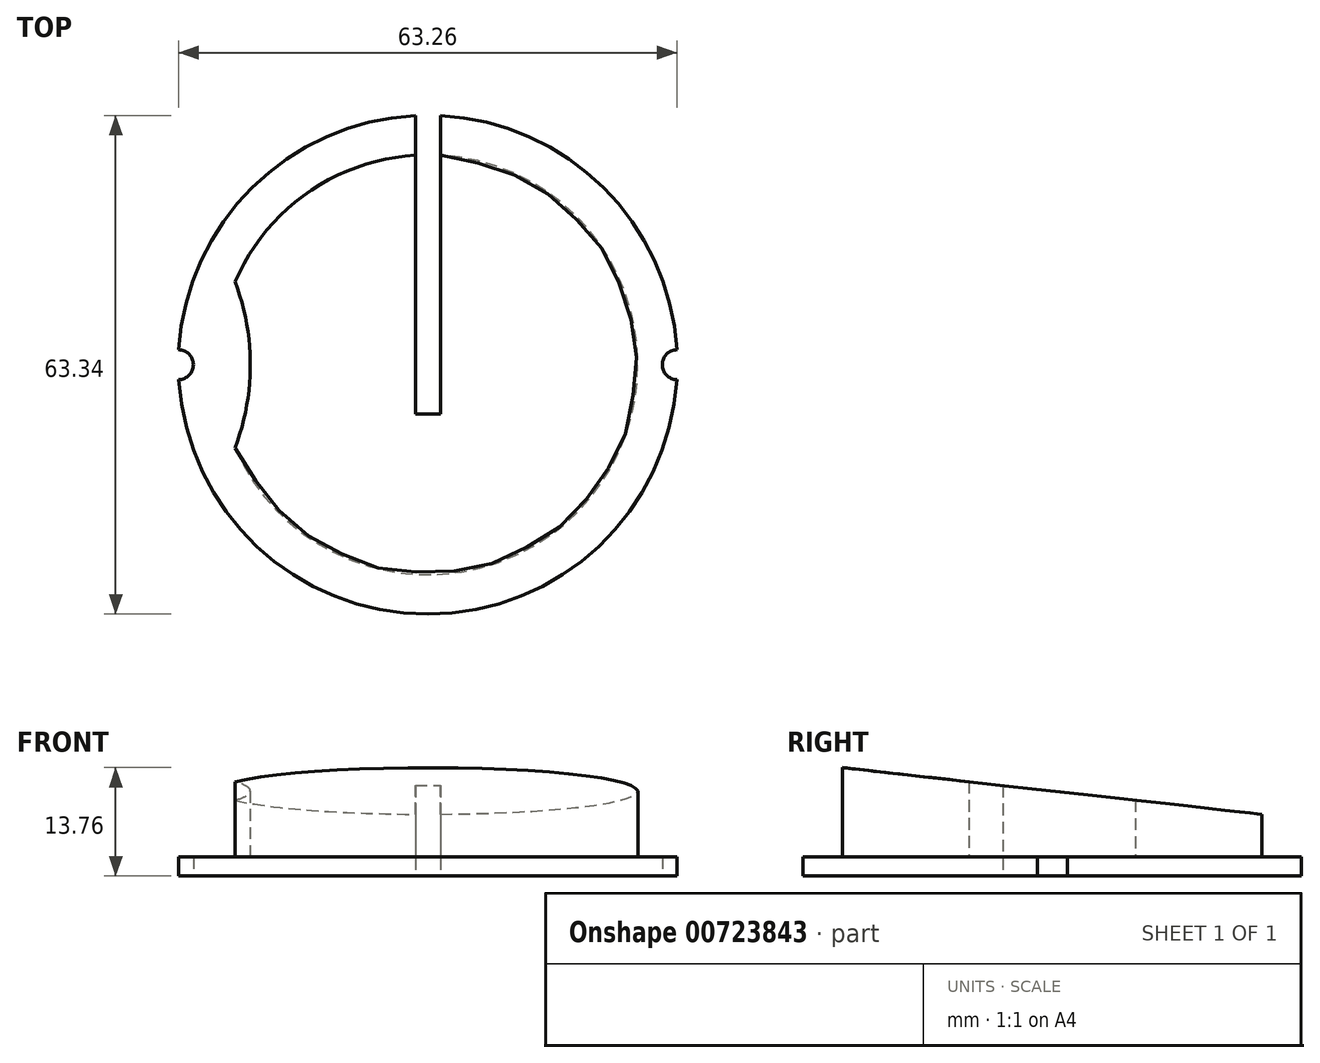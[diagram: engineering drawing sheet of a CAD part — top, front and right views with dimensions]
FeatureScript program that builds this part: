
annotation { "Feature Type Name" : "Feature", "Feature Type Description" : "" }
export const myFeature = defineFeature(function(context is Context, id is Id, definition is map)
    precondition{}
    {
        {
            var Q0;
            Q0=qCreatedBy(makeId("Top.planeOp"),FACE);
            var sketch = newSketch(context, id + "F0", { "sketchPlane" : qUnion([Q0])});
            skArc(sketch, "E0", {"start": v(31.63, 1.9) * mm, "mid": v(0, 31.69) * mm, "end": v(-31.63, 1.9) * mm});
            skArc(sketch, "E1", {"start": v(-31.63, -1.9) * mm, "mid": v(-29.78, 0) * mm, "end": v(-31.63, 1.9) * mm});
            skArc(sketch, "E2", {"start": v(31.63, 1.9) * mm, "mid": v(29.78, 0) * mm, "end": v(31.63, -1.9) * mm});
            skArc(sketch, "E3.trimOffspring", {"start": v(-31.63, -1.9) * mm, "mid": v(0, -31.69) * mm, "end": v(31.63, -1.9) * mm});
            skSolve(sketch);
        }
        {
            var Q0;
            Q0=makeQuery(id+"F0.imprint","IMPRINT",FACE,{"disambiguationData":[TD([[makeQuery(id+"F0.imprint","IMPRINT",EDGE,{"derivedFrom":sQuery(id+"F0.wireOp",EDGE,"E0")}),1.0]])]});
            extrude(context, id + "F1", {"entities" : qUnion([Q0]), "depth" : 2.41 * mm, "offsetDistance" : 25.4 * mm});
        }
        {
            var Q0;
            Q0=makeQuery(id+"F1.opExtrude","CAP_FACE",FACE,{"disambiguationData":[OSD([sQuery(id+"F0.wireOp",EDGE,"E0"),sQuery(id+"F0.wireOp",EDGE,"E1"),sQuery(id+"F0.wireOp",EDGE,"E2"),sQuery(id+"F0.wireOp",EDGE,"E3.trimOffspring")])],"isStart":false});
            var sketch = newSketch(context, id + "F2", { "sketchPlane" : qUnion([Q0])});
            skArc(sketch, "E4", {"start": v(-24.49, -10.57) * mm, "mid": v(26.67, 0) * mm, "end": v(-24.49, 10.57) * mm});
            skCircle(sketch, "E5", {"center": v(-26.67, 0) * mm, "radius": 10.8 * mm, "construction": true});
            skCircle(sketch, "E6", {"center": v(-26.67, 0) * mm, "radius": 4.13 * mm, "construction": true});
            skArc(sketch, "E7", {"start": v(-24.49, -10.57) * mm, "mid": v(-22.54, 0) * mm, "end": v(-24.49, 10.57) * mm});
            skPoint(sketch, "E7.first.point", {"position": v(-24.49, 10.57) * mm});
            skPoint(sketch, "E7.second.point", {"position": v(-22.54, 0) * mm});
            skPoint(sketch, "E7.third.point", {"position": v(-24.49, -10.57) * mm});
            skSolve(sketch);
        }
        {
            var Q0;
            Q0=makeQuery(id+"F2.imprint","IMPRINT",FACE,{"disambiguationData":[TD([[makeQuery(id+"F2.imprint","IMPRINT",EDGE,{"derivedFrom":sQuery(id+"F2.wireOp",EDGE,"E4")}),1.0]])]});
            extrude(context, id + "F3", {"entities" : qUnion([Q0]), "operationType" : NewBodyOperationType.ADD, "depth" : 25.4 * mm, "offsetDistance" : 25.4 * mm});
        }
        {
            var Q0;
            Q0=qCreatedBy(makeId("Right.planeOp"),FACE);
            var sketch = newSketch(context, id + "F4", { "sketchPlane" : qUnion([Q0])});
            skLineSegment(sketch, "E8", {"start": v(-28.57, 13.97) * mm, "end": v(28.57, 7.62) * mm});
            skLineSegment(sketch, "E9", {"start": v(28.57, 7.62) * mm, "end": v(28.57, 36.8) * mm});
            skLineSegment(sketch, "E10", {"start": v(28.57, 36.8) * mm, "end": v(-28.58, 36.8) * mm});
            skLineSegment(sketch, "E11", {"start": v(-28.58, 36.8) * mm, "end": v(-28.57, 13.97) * mm});
            skSolve(sketch);
        }
        {
            var Q0;
            Q0=makeQuery(id+"F4.imprint","IMPRINT",FACE,{"disambiguationData":[TD([[makeQuery(id+"F4.imprint","IMPRINT",EDGE,{"derivedFrom":sQuery(id+"F4.wireOp",EDGE,"E8")}),1.0]])]});
            extrude(context, id + "F5", {"entities" : qUnion([Q0]), "operationType" : NewBodyOperationType.REMOVE, "endBound" : BoundingType.SYMMETRIC, "oppositeDirection" : true, "depth" : 63.5 * mm, "offsetDistance" : 25.4 * mm});
        }
        {
            var Q0;
            Q0=makeQuery(id+"F1.opExtrude","CAP_FACE",FACE,{"disambiguationData":[OSD([sQuery(id+"F0.wireOp",EDGE,"E0"),sQuery(id+"F0.wireOp",EDGE,"E1"),sQuery(id+"F0.wireOp",EDGE,"E2"),sQuery(id+"F0.wireOp",EDGE,"E3.trimOffspring")])],"isStart":true});
            var sketch = newSketch(context, id + "F6", { "sketchPlane" : qUnion([Q0])});
            skLineSegment(sketch, "E12.bottom", {"start": v(-1.59, -44.51) * mm, "end": v(1.59, -44.51) * mm});
            skLineSegment(sketch, "E12.top", {"start": v(-1.59, 6.29) * mm, "end": v(1.59, 6.29) * mm});
            skLineSegment(sketch, "E12.left", {"start": v(-1.59, -44.51) * mm, "end": v(-1.59, 6.29) * mm});
            skLineSegment(sketch, "E12.right", {"start": v(1.59, -44.51) * mm, "end": v(1.59, 6.29) * mm});
            skSolve(sketch);
        }
        {
            var Q0;
            {var subQ0=sQuery(id+"F6.wireOp",EDGE,"E12.top");Q0=makeQuery(id+"F6.imprint","IMPRINT",FACE,{"disambiguationData":[TD([[makeQuery(id+"F6.imprint","IMPRINT",EDGE,{"derivedFrom":subQ0}),-1.0]])]});}
            var Q1;
            {var subQ0=sQuery(id+"F6.wireOp",EDGE,"E12.bottom");Q1=makeQuery(id+"F6.imprint","IMPRINT",FACE,{"disambiguationData":[TD([[makeQuery(id+"F6.imprint","IMPRINT",EDGE,{"derivedFrom":subQ0}),1.0]])]});}
            extrude(context, id + "F7", {"entities" : qUnion([Q0, Q1]), "operationType" : NewBodyOperationType.REMOVE, "oppositeDirection" : true, "depth" : 25.4 * mm, "offsetDistance" : 25.4 * mm});
        }
    });
